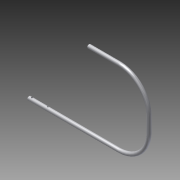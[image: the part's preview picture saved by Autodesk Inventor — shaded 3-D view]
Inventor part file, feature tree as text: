
AUTODESK INVENTOR PART (.ipt)
format: ipt  version: 2014 (Build 180170000, 170)  size: 140,288 bytes
history: native  units: in
note: dims shown in document units (in); Inventor stores cm internally (conversion verified against a paired STEP export)
features: sketch x3, sweep x1, plane x1, extrude x1
ambient origin geometry x8: Origin, YZ Plane, XZ Plane, XY Plane, X Axis, Y Axis, Z Axis, Center Point
bodies: Solid1 (feature_tree)
feature tree (6):
  sweep  "Sweep1"
  plane  "Work Plane1"
  extrude  "Extrusion1"  Depth=4.0in
  sketch  "Sketch1"  dims[d0=12.0in d1=4.0in]
  sketch  "Sketch2"  dims[d2=2.0in d3=4.0in]
  sketch  "Sketch3"  dims[d4=4.0in d5=0.5in d6=0.0in d7=25.0in d8=0.375in d9=0.164in d10=2.5in d11=0.25in d12=1.0in d13=0.0in d14=0.194in d15=0.375in d16=0.25in]
